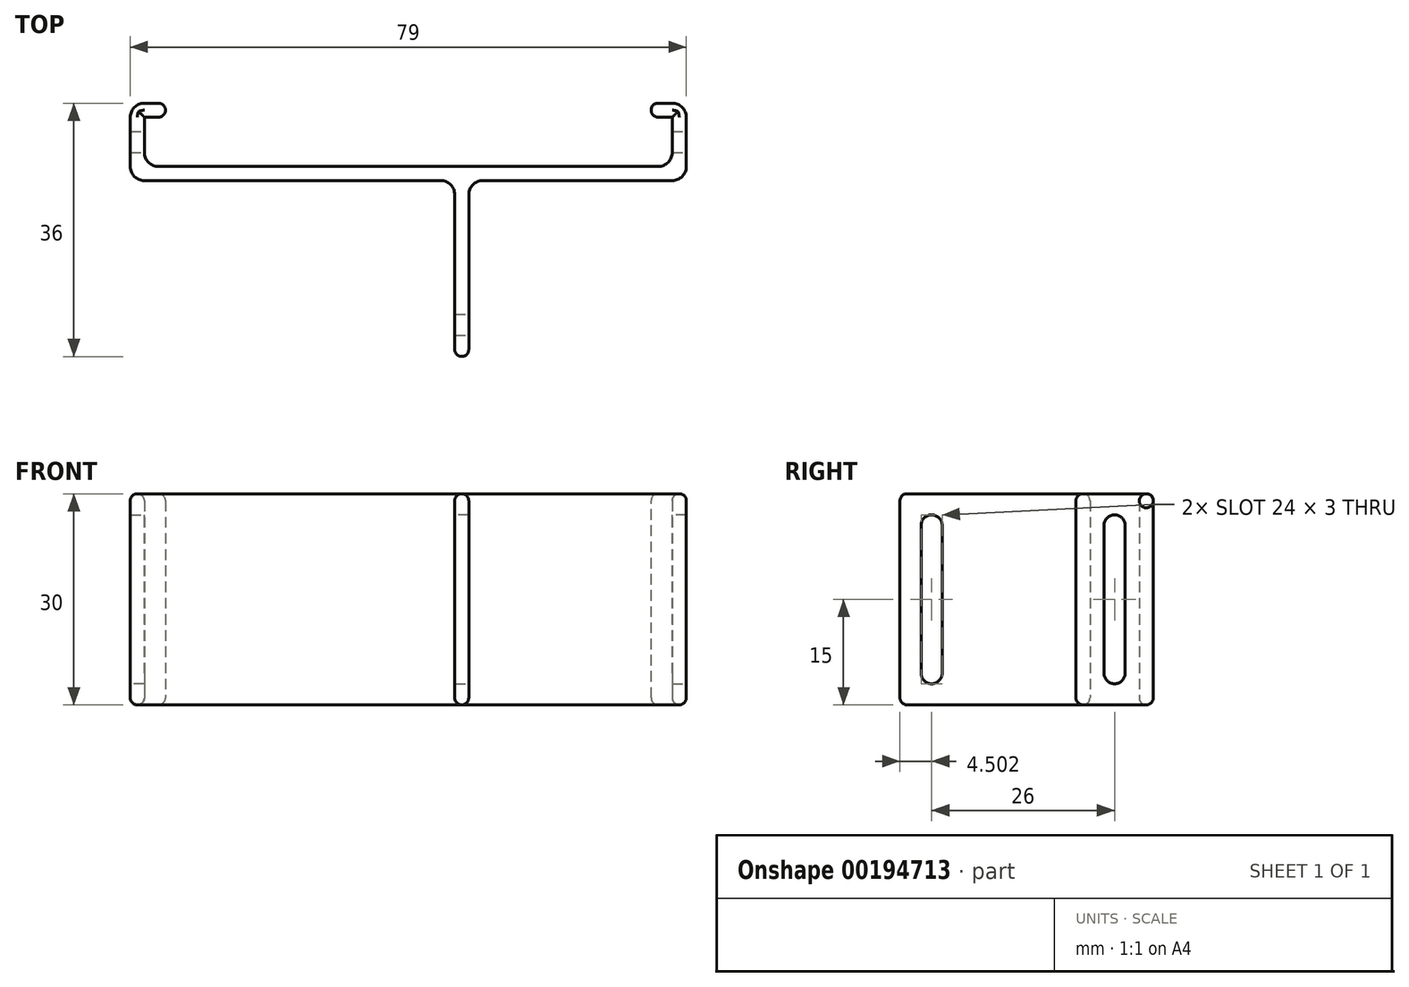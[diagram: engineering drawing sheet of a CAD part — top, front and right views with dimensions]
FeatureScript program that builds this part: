
annotation { "Feature Type Name" : "Feature", "Feature Type Description" : "" }
export const myFeature = defineFeature(function(context is Context, id is Id, definition is map)
    precondition{}
    {
        {
            var Q0;
            Q0=qCreatedBy(makeId("Top.planeOp"),FACE);
            var sketch = newSketch(context, id + "F0", { "sketchPlane" : qUnion([Q0])});
            skLineSegment(sketch, "E0.bottom", {"start": v(-52.04, 0.3) * mm, "end": v(22.96, 0.3) * mm});
            skLineSegment(sketch, "E0.top", {"start": v(-52.04, -1.7) * mm, "end": v(22.96, -1.7) * mm});
            skLineSegment(sketch, "E0.left", {"start": v(-52.04, 0.3) * mm, "end": v(-52.04, -1.7) * mm});
            skLineSegment(sketch, "E0.right", {"start": v(22.96, 0.3) * mm, "end": v(22.96, -1.7) * mm});
            skLineSegment(sketch, "E1.bottom", {"start": v(-52.04, -1.7) * mm, "end": v(-54.04, -1.7) * mm});
            skLineSegment(sketch, "E1.top", {"start": v(-52.04, 7.3) * mm, "end": v(-54.04, 7.3) * mm});
            skLineSegment(sketch, "E1.left", {"start": v(-52.04, -1.7) * mm, "end": v(-52.04, 7.3) * mm});
            skLineSegment(sketch, "E1.right", {"start": v(-54.04, -1.7) * mm, "end": v(-54.04, 7.3) * mm});
            skLineSegment(sketch, "E2.bottom", {"start": v(22.96, -1.7) * mm, "end": v(24.96, -1.7) * mm});
            skLineSegment(sketch, "E2.top", {"start": v(22.96, 7.3) * mm, "end": v(24.96, 7.3) * mm});
            skLineSegment(sketch, "E2.left", {"start": v(22.96, -1.7) * mm, "end": v(22.96, 7.3) * mm});
            skLineSegment(sketch, "E2.right", {"start": v(24.96, -1.7) * mm, "end": v(24.96, 7.3) * mm});
            skLineSegment(sketch, "E3.bottom", {"start": v(-54.04, 7.3) * mm, "end": v(-49.04, 7.3) * mm});
            skLineSegment(sketch, "E3.top", {"start": v(-54.04, 9.3) * mm, "end": v(-49.04, 9.3) * mm});
            skLineSegment(sketch, "E3.left", {"start": v(-54.04, 7.3) * mm, "end": v(-54.04, 9.3) * mm});
            skLineSegment(sketch, "E3.right", {"start": v(-49.04, 7.3) * mm, "end": v(-49.04, 9.3) * mm});
            skLineSegment(sketch, "E4.bottom", {"start": v(24.96, 7.3) * mm, "end": v(19.96, 7.3) * mm});
            skLineSegment(sketch, "E4.top", {"start": v(24.96, 9.3) * mm, "end": v(19.96, 9.3) * mm});
            skLineSegment(sketch, "E4.left", {"start": v(24.96, 7.3) * mm, "end": v(24.96, 9.3) * mm});
            skLineSegment(sketch, "E4.right", {"start": v(19.96, 7.3) * mm, "end": v(19.96, 9.3) * mm});
            skLineSegment(sketch, "E5.bottom", {"start": v(-7.94, -1.7) * mm, "end": v(-5.94, -1.7) * mm});
            skLineSegment(sketch, "E5.top", {"start": v(-7.94, -26.7) * mm, "end": v(-5.94, -26.7) * mm});
            skLineSegment(sketch, "E5.left", {"start": v(-7.94, -1.7) * mm, "end": v(-7.94, -26.7) * mm});
            skLineSegment(sketch, "E5.right", {"start": v(-5.94, -1.7) * mm, "end": v(-5.94, -26.7) * mm});
            skSolve(sketch);
        }
        {
            var Q0;
            Q0=qSketchRegion(id+"F0",true);
            extrude(context, id + "F1", {"entities" : qUnion([Q0]), "depth" : 30 * mm});
        }
        {
            var Q0;
            Q0=makeQuery(id+"F1.opExtrude","SWEPT_EDGE",EDGE,{"disambiguationData":[OSD([sQuery(id+"F0.wireOp",EDGE,"E4.top"),sQuery(id+"F0.wireOp",EDGE,"E4.right")])]});
            var Q1;
            Q1=makeQuery(id+"F1.opExtrude","SWEPT_EDGE",EDGE,{"disambiguationData":[OSD([sQuery(id+"F0.wireOp",EDGE,"E4.bottom"),sQuery(id+"F0.wireOp",EDGE,"E4.right")])]});
            var Q2;
            Q2=makeQuery(id+"F1.opExtrude","SWEPT_EDGE",EDGE,{"disambiguationData":[OSD([sQuery(id+"F0.wireOp",EDGE,"E3.bottom"),sQuery(id+"F0.wireOp",EDGE,"E3.right")])]});
            var Q3;
            Q3=makeQuery(id+"F1.opExtrude","SWEPT_EDGE",EDGE,{"disambiguationData":[OSD([sQuery(id+"F0.wireOp",EDGE,"E3.top"),sQuery(id+"F0.wireOp",EDGE,"E3.right")])]});
            var Q4;
            Q4=makeQuery(id+"F1.opExtrude","SWEPT_EDGE",EDGE,{"disambiguationData":[OSD([sQuery(id+"F0.wireOp",EDGE,"cbmLmww0-s3Uw-X8MJ-5Prn-tQJUQLKUa4ud.bottom"),sQuery(id+"F0.wireOp",EDGE,"cbmLmww0-s3Uw-X8MJ-5Prn-tQJUQLKUa4ud.right")])]});
            var Q5;
            Q5=makeQuery(id+"F1.opExtrude","SWEPT_EDGE",EDGE,{"disambiguationData":[OSD([sQuery(id+"F0.wireOp",EDGE,"cbmLmww0-s3Uw-X8MJ-5Prn-tQJUQLKUa4ud.top"),sQuery(id+"F0.wireOp",EDGE,"cbmLmww0-s3Uw-X8MJ-5Prn-tQJUQLKUa4ud.right")])]});
            var Q6;
            Q6=makeQuery(id+"F1.opExtrude","SWEPT_EDGE",EDGE,{"disambiguationData":[OSD([sQuery(id+"F0.wireOp",EDGE,"k5Te9g92-1lri-thvY-4GBi-rrRn1ozToLpT"),sQuery(id+"F0.wireOp",EDGE,"1oixEqxv-xunt-Uujw-OjL6-xhiZLuC5YG3Y")])]});
            var Q7;
            Q7=makeQuery(id+"F1.opExtrude","SWEPT_EDGE",EDGE,{"disambiguationData":[OSD([sQuery(id+"F0.wireOp",EDGE,"SKFn4g7b-b4ij-pO12-mW4x-pk4dDxGWjY4T"),sQuery(id+"F0.wireOp",EDGE,"1oixEqxv-xunt-Uujw-OjL6-xhiZLuC5YG3Y")])]});
            var Q8;
            Q8=makeQuery(id+"F1.opExtrude","SWEPT_EDGE",EDGE,{"disambiguationData":[OSD([sQuery(id+"F0.wireOp",EDGE,"qTu8kI1h-vp8o-eVCS-FlEb-47N6jWhdIGku"),sQuery(id+"F0.wireOp",EDGE,"B1kFFgH6-ISfz-WU8D-3Uqx-DWIzix366O4G")])]});
            var Q9;
            Q9=makeQuery(id+"F1.opExtrude","SWEPT_EDGE",EDGE,{"disambiguationData":[OSD([sQuery(id+"F0.wireOp",EDGE,"B1kFFgH6-ISfz-WU8D-3Uqx-DWIzix366O4G"),sQuery(id+"F0.wireOp",EDGE,"b87Un2YB-kZn9-Zs8O-EuaL-8bBbOIus6pSa")])]});
            var Q10;
            Q10=makeQuery(id+"F1.opExtrude","SWEPT_EDGE",EDGE,{"disambiguationData":[OSD([sQuery(id+"F0.wireOp",EDGE,"E5.top"),sQuery(id+"F0.wireOp",EDGE,"E5.right")])]});
            var Q11;
            Q11=makeQuery(id+"F1.opExtrude","SWEPT_EDGE",EDGE,{"disambiguationData":[OSD([sQuery(id+"F0.wireOp",EDGE,"E5.top"),sQuery(id+"F0.wireOp",EDGE,"E5.left")])]});
            fillet(context, id + "F2", {"entities" : qUnion([Q0, Q1, Q2, Q3, Q4, Q5, Q6, Q7, Q8, Q9, Q10, Q11]), "radius" : 1 * mm, "tangentPropagation" : true, "allowEdgeOverflow" : false});
        }
        {
            var Q0;
            Q0=makeQuery(id+"F1.opExtrude","SWEPT_EDGE",EDGE,{"disambiguationData":[OSD([sQuery(id+"F0.wireOp",EDGE,"E3.top"),sQuery(id+"F0.wireOp",EDGE,"E3.left")])]});
            var Q1;
            Q1=makeQuery(id+"F1.opExtrude","SWEPT_EDGE",EDGE,{"disambiguationData":[OSD([sQuery(id+"F0.wireOp",EDGE,"E1.bottom"),sQuery(id+"F0.wireOp",EDGE,"E1.right")])]});
            var Q2;
            Q2=makeQuery(id+"F1.opExtrude","SWEPT_EDGE",EDGE,{"disambiguationData":[OSD([sQuery(id+"F0.wireOp",EDGE,"E2.bottom"),sQuery(id+"F0.wireOp",EDGE,"E2.right")])]});
            var Q3;
            Q3=makeQuery(id+"F1.opExtrude","SWEPT_EDGE",EDGE,{"disambiguationData":[OSD([sQuery(id+"F0.wireOp",EDGE,"E4.top"),sQuery(id+"F0.wireOp",EDGE,"E4.left")])]});
            var Q4;
            Q4=makeQuery(id+"F1.opExtrude","SWEPT_EDGE",EDGE,{"disambiguationData":[OSD([sQuery(id+"F0.wireOp",EDGE,"cbmLmww0-s3Uw-X8MJ-5Prn-tQJUQLKUa4ud.top"),sQuery(id+"F0.wireOp",EDGE,"cbmLmww0-s3Uw-X8MJ-5Prn-tQJUQLKUa4ud.left")])]});
            var Q5;
            Q5=makeQuery(id+"F1.opExtrude","SWEPT_EDGE",EDGE,{"disambiguationData":[OSD([sQuery(id+"F0.wireOp",EDGE,"E0.top"),sQuery(id+"F0.wireOp",EDGE,"DhNBHtjC-mmht-2zA3-qtbX-Vav0KUQkQ3ZT.bottom"),sQuery(id+"F0.wireOp",EDGE,"DhNBHtjC-mmht-2zA3-qtbX-Vav0KUQkQ3ZT.right")])]});
            var Q6;
            Q6=makeQuery(id+"F1.opExtrude","SWEPT_EDGE",EDGE,{"disambiguationData":[OSD([sQuery(id+"F0.wireOp",EDGE,"E0.top"),sQuery(id+"F0.wireOp",EDGE,"DhNBHtjC-mmht-2zA3-qtbX-Vav0KUQkQ3ZT.bottom"),sQuery(id+"F0.wireOp",EDGE,"DhNBHtjC-mmht-2zA3-qtbX-Vav0KUQkQ3ZT.left")])]});
            var Q7;
            Q7=makeQuery(id+"F1.opExtrude","SWEPT_EDGE",EDGE,{"disambiguationData":[OSD([sQuery(id+"F0.wireOp",EDGE,"DhNBHtjC-mmht-2zA3-qtbX-Vav0KUQkQ3ZT.right"),sQuery(id+"F0.wireOp",EDGE,"cbmLmww0-s3Uw-X8MJ-5Prn-tQJUQLKUa4ud.bottom")])]});
            var Q8;
            Q8=makeQuery(id+"F1.opExtrude","SWEPT_EDGE",EDGE,{"disambiguationData":[OSD([sQuery(id+"F0.wireOp",EDGE,"E0.bottom"),sQuery(id+"F0.wireOp",EDGE,"E1.left")])]});
            var Q9;
            Q9=makeQuery(id+"F1.opExtrude","SWEPT_EDGE",EDGE,{"disambiguationData":[OSD([sQuery(id+"F0.wireOp",EDGE,"E0.bottom"),sQuery(id+"F0.wireOp",EDGE,"E2.left")])]});
            fillet(context, id + "F3", {"entities" : qUnion([Q0, Q1, Q2, Q3, Q4, Q5, Q6, Q7, Q8, Q9]), "radius" : 2 * mm, "tangentPropagation" : true, "allowEdgeOverflow" : false});
        }
        {
            var Q0;
            Q0=makeQuery(id+"F1.opExtrude","CAP_EDGE",EDGE,{"disambiguationData":[OSD([sQuery(id+"F0.wireOp",EDGE,"k5Te9g92-1lri-thvY-4GBi-rrRn1ozToLpT")])],"isStart":false});
            var Q1;
            Q1=makeQuery(id+"F1.opExtrude","CAP_EDGE",EDGE,{"disambiguationData":[OSD([sQuery(id+"F0.wireOp",EDGE,"E0.bottom")])],"isStart":false});
            var Q2;
            Q2=makeQuery(id+"F1.opExtrude","CAP_EDGE",EDGE,{"disambiguationData":[OSD([sQuery(id+"F0.wireOp",EDGE,"SKFn4g7b-b4ij-pO12-mW4x-pk4dDxGWjY4T")])],"isStart":true});
            var Q3;
            Q3=makeQuery(id+"F1.opExtrude","CAP_EDGE",EDGE,{"disambiguationData":[OSD([sQuery(id+"F0.wireOp",EDGE,"E0.bottom")])],"isStart":true});
            var Q4;
            Q4=makeQuery(id+"F1.opExtrude","CAP_EDGE",EDGE,{"disambiguationData":[OSD([sQuery(id+"F0.wireOp",EDGE,"E5.right")])],"isStart":false});
            var Q5;
            Q5=makeQuery(id+"F1.opExtrude","CAP_EDGE",EDGE,{"disambiguationData":[OSD([sQuery(id+"F0.wireOp",EDGE,"E5.right")])],"isStart":true});
            fillet(context, id + "F4", {"entities" : qUnion([Q0, Q1, Q2, Q3, Q4, Q5]), "radius" : 1 * mm, "tangentPropagation" : true, "allowEdgeOverflow" : false});
        }
        {
            var Q0;
            Q0=makeQuery(id+"F1.opExtrude","SWEPT_FACE",FACE,{"disambiguationData":[OSD([sQuery(id+"F0.wireOp",EDGE,"E5.right")])]});
            var sketch = newSketch(context, id + "F5", { "sketchPlane" : qUnion([Q0])});
            skLineSegment(sketch, "E6.bottom", {"start": v(-23.7, 27) * mm, "end": v(-20.7, 27) * mm});
            skLineSegment(sketch, "E6.top", {"start": v(-23.7, 3) * mm, "end": v(-20.7, 3) * mm});
            skLineSegment(sketch, "E6.left", {"start": v(-23.7, 27) * mm, "end": v(-23.7, 3) * mm});
            skLineSegment(sketch, "E6.right", {"start": v(-20.7, 27) * mm, "end": v(-20.7, 3) * mm});
            skLineSegment(sketch, "E7", {"start": v(-22.2, 27) * mm, "end": v(-22.2, 29) * mm, "construction": true});
            skLineSegment(sketch, "E8", {"start": v(-22.2, 3) * mm, "end": v(-22.2, 1) * mm, "construction": true});
            skLineSegment(sketch, "E9", {"start": v(-23.7, 15) * mm, "end": v(-25.7, 15) * mm, "construction": true});
            skSolve(sketch);
        }
        {
            var Q0;
            Q0=makeQuery(id+"F5.imprint","IMPRINT",FACE,{"disambiguationData":[TD([[makeQuery(id+"F5.imprint","IMPRINT",EDGE,{"derivedFrom":sQuery(id+"F5.wireOp",EDGE,"E6.bottom")}),-1.0]])]});
            extrude(context, id + "F6", {"entities" : qUnion([Q0]), "operationType" : NewBodyOperationType.REMOVE, "endBound" : BoundingType.THROUGH_ALL, "oppositeDirection" : true, "depth" : 25 * mm});
        }
        {
            var Q0;
            Q0=makeQuery(id+"F1.opExtrude","SWEPT_FACE",FACE,{"disambiguationData":[OSD([sQuery(id+"F0.wireOp",EDGE,"E2.right"),sQuery(id+"F0.wireOp",EDGE,"E4.left")])]});
            var sketch = newSketch(context, id + "F7", { "sketchPlane" : qUnion([Q0])});
            skLineSegment(sketch, "E10.bottom", {"start": v(2.3, 27) * mm, "end": v(5.3, 27) * mm});
            skLineSegment(sketch, "E10.top", {"start": v(2.3, 3) * mm, "end": v(5.3, 3) * mm});
            skLineSegment(sketch, "E10.left", {"start": v(2.3, 27) * mm, "end": v(2.3, 3) * mm});
            skLineSegment(sketch, "E10.right", {"start": v(5.3, 27) * mm, "end": v(5.3, 3) * mm});
            skLineSegment(sketch, "E11", {"start": v(3.8, 27) * mm, "end": v(3.8, 29) * mm, "construction": true});
            skLineSegment(sketch, "E12", {"start": v(3.8, 3) * mm, "end": v(3.8, 1) * mm, "construction": true});
            skLineSegment(sketch, "E13", {"start": v(5.3, 15) * mm, "end": v(7.3, 15) * mm, "construction": true});
            skLineSegment(sketch, "E14", {"start": v(2.3, 15) * mm, "end": v(0.3, 15) * mm, "construction": true});
            skSolve(sketch);
        }
        {
            var Q0;
            Q0=makeQuery(id+"F7.imprint","IMPRINT",FACE,{"disambiguationData":[TD([[makeQuery(id+"F7.imprint","IMPRINT",EDGE,{"derivedFrom":sQuery(id+"F7.wireOp",EDGE,"E10.bottom")}),-1.0]])]});
            extrude(context, id + "F8", {"entities" : qUnion([Q0]), "operationType" : NewBodyOperationType.REMOVE, "endBound" : BoundingType.THROUGH_ALL, "oppositeDirection" : true, "depth" : 25 * mm});
        }
        {
            var Q0;
            {var subQ0=sQuery(id+"F7.wireOp",EDGE,"E10.top");var subQ1=sQuery(id+"F7.wireOp",EDGE,"E10.right");Q0=makeQuery(id+"F8.boolean.opBoolean","COPY",EDGE,{"disambiguationData":[TD([makeQuery(id+"F1.opExtrude","SWEPT_FACE",FACE,{"disambiguationData":[OSD([sQuery(id+"F0.wireOp",EDGE,"E2.left")])]})])],"derivedFrom":makeQuery(id+"F8.opExtrude","SWEPT_EDGE",EDGE,{"disambiguationData":[OSD([subQ0,subQ1])]})});}
            var Q1;
            {var subQ0=sQuery(id+"F7.wireOp",EDGE,"E10.bottom");var subQ1=sQuery(id+"F7.wireOp",EDGE,"E10.right");Q1=makeQuery(id+"F8.boolean.opBoolean","COPY",EDGE,{"disambiguationData":[TD([makeQuery(id+"F1.opExtrude","SWEPT_FACE",FACE,{"disambiguationData":[OSD([sQuery(id+"F0.wireOp",EDGE,"E2.left")])]})])],"derivedFrom":makeQuery(id+"F8.opExtrude","SWEPT_EDGE",EDGE,{"disambiguationData":[OSD([subQ0,subQ1])]})});}
            var Q2;
            Q2=makeQuery(id+"F6.boolean.opBoolean","COPY",EDGE,{"derivedFrom":makeQuery(id+"F6.opExtrude","SWEPT_EDGE",EDGE,{"disambiguationData":[OSD([sQuery(id+"F5.wireOp",EDGE,"E6.top"),sQuery(id+"F5.wireOp",EDGE,"E6.right")])]})});
            var Q3;
            Q3=makeQuery(id+"F6.boolean.opBoolean","COPY",EDGE,{"derivedFrom":makeQuery(id+"F6.opExtrude","SWEPT_EDGE",EDGE,{"disambiguationData":[OSD([sQuery(id+"F5.wireOp",EDGE,"E6.bottom"),sQuery(id+"F5.wireOp",EDGE,"E6.right")])]})});
            var Q4;
            {var subQ0=sQuery(id+"F7.wireOp",EDGE,"E10.top");var subQ1=sQuery(id+"F0.wireOp",EDGE,"E1.left");var subQ2=sQuery(id+"F7.wireOp",EDGE,"E10.left");Q4=makeQuery(id+"F8.boolean.opBoolean","COPY",EDGE,{"disambiguationData":[TD([makeQuery(id+"F1.opExtrude","SWEPT_FACE",FACE,{"disambiguationData":[OSD([subQ1])]})])],"derivedFrom":makeQuery(id+"F8.opExtrude","SWEPT_EDGE",EDGE,{"disambiguationData":[OSD([subQ0,subQ2])]})});}
            var Q5;
            {var subQ0=sQuery(id+"F0.wireOp",EDGE,"E2.left");var subQ1=sQuery(id+"F7.wireOp",EDGE,"E10.top");var subQ2=sQuery(id+"F7.wireOp",EDGE,"E10.left");Q5=makeQuery(id+"F8.boolean.opBoolean","COPY",EDGE,{"disambiguationData":[TD([makeQuery(id+"F1.opExtrude","SWEPT_FACE",FACE,{"disambiguationData":[OSD([subQ0])]})])],"derivedFrom":makeQuery(id+"F8.opExtrude","SWEPT_EDGE",EDGE,{"disambiguationData":[OSD([subQ1,subQ2])]})});}
            var Q6;
            Q6=makeQuery(id+"F6.boolean.opBoolean","COPY",EDGE,{"derivedFrom":makeQuery(id+"F6.opExtrude","SWEPT_EDGE",EDGE,{"disambiguationData":[OSD([sQuery(id+"F5.wireOp",EDGE,"E6.top"),sQuery(id+"F5.wireOp",EDGE,"E6.left")])]})});
            var Q7;
            {var subQ0=sQuery(id+"F0.wireOp",EDGE,"E2.left");var subQ1=sQuery(id+"F7.wireOp",EDGE,"E10.bottom");var subQ2=sQuery(id+"F7.wireOp",EDGE,"E10.left");Q7=makeQuery(id+"F8.boolean.opBoolean","COPY",EDGE,{"disambiguationData":[TD([makeQuery(id+"F1.opExtrude","SWEPT_FACE",FACE,{"disambiguationData":[OSD([subQ0])]})])],"derivedFrom":makeQuery(id+"F8.opExtrude","SWEPT_EDGE",EDGE,{"disambiguationData":[OSD([subQ1,subQ2])]})});}
            var Q8;
            {var subQ0=sQuery(id+"F7.wireOp",EDGE,"E10.bottom");var subQ1=sQuery(id+"F0.wireOp",EDGE,"E1.left");var subQ2=sQuery(id+"F7.wireOp",EDGE,"E10.left");Q8=makeQuery(id+"F8.boolean.opBoolean","COPY",EDGE,{"disambiguationData":[TD([makeQuery(id+"F1.opExtrude","SWEPT_FACE",FACE,{"disambiguationData":[OSD([subQ1])]})])],"derivedFrom":makeQuery(id+"F8.opExtrude","SWEPT_EDGE",EDGE,{"disambiguationData":[OSD([subQ0,subQ2])]})});}
            var Q9;
            Q9=makeQuery(id+"F6.boolean.opBoolean","COPY",EDGE,{"derivedFrom":makeQuery(id+"F6.opExtrude","SWEPT_EDGE",EDGE,{"disambiguationData":[OSD([sQuery(id+"F5.wireOp",EDGE,"E6.bottom"),sQuery(id+"F5.wireOp",EDGE,"E6.left")])]})});
            var Q10;
            {var subQ0=sQuery(id+"F7.wireOp",EDGE,"E10.top");var subQ1=sQuery(id+"F7.wireOp",EDGE,"E10.right");Q10=makeQuery(id+"F8.boolean.opBoolean","COPY",EDGE,{"disambiguationData":[TD([makeQuery(id+"F1.opExtrude","SWEPT_FACE",FACE,{"disambiguationData":[OSD([sQuery(id+"F0.wireOp",EDGE,"E1.left")])]})])],"derivedFrom":makeQuery(id+"F8.opExtrude","SWEPT_EDGE",EDGE,{"disambiguationData":[OSD([subQ0,subQ1])]})});}
            var Q11;
            {var subQ0=sQuery(id+"F7.wireOp",EDGE,"E10.bottom");var subQ1=sQuery(id+"F7.wireOp",EDGE,"E10.right");Q11=makeQuery(id+"F8.boolean.opBoolean","COPY",EDGE,{"disambiguationData":[TD([makeQuery(id+"F1.opExtrude","SWEPT_FACE",FACE,{"disambiguationData":[OSD([sQuery(id+"F0.wireOp",EDGE,"E1.left")])]})])],"derivedFrom":makeQuery(id+"F8.opExtrude","SWEPT_EDGE",EDGE,{"disambiguationData":[OSD([subQ0,subQ1])]})});}
            fillet(context, id + "F9", {"entities" : qUnion([Q0, Q1, Q2, Q3, Q4, Q5, Q6, Q7, Q8, Q9, Q10, Q11]), "radius" : 1.5 * mm, "tangentPropagation" : true, "allowEdgeOverflow" : false});
        }
    });
